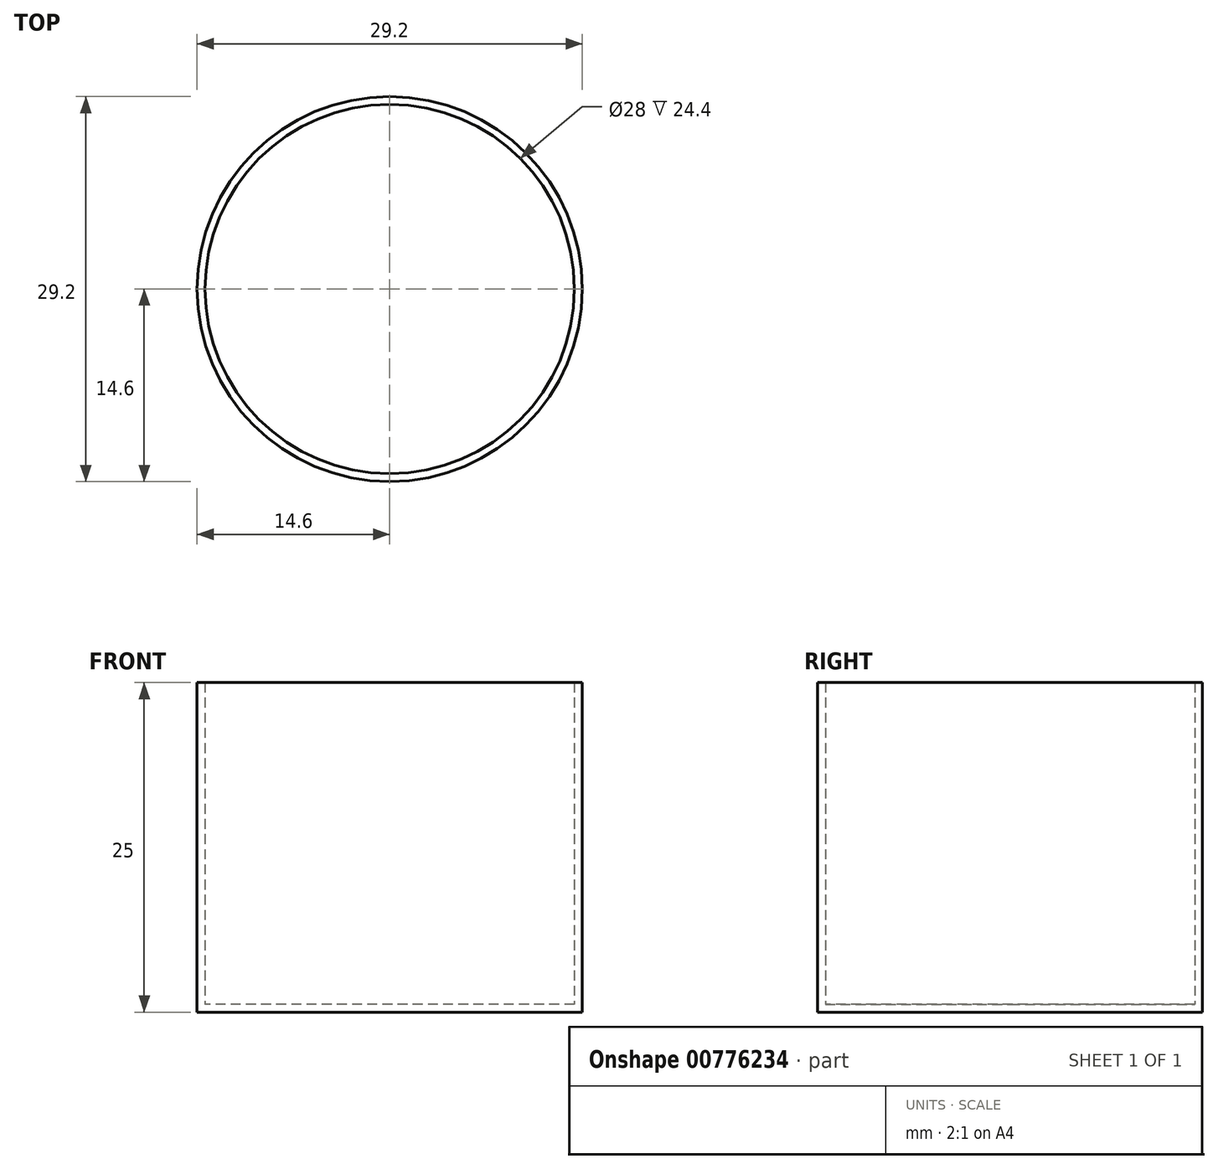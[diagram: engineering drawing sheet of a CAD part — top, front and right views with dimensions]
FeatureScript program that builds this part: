
annotation { "Feature Type Name" : "Feature", "Feature Type Description" : "" }
export const myFeature = defineFeature(function(context is Context, id is Id, definition is map)
    precondition{}
    {
        {
            var Q0;
            Q0=qCreatedBy(makeId("Top.planeOp"),FACE);
            var sketch = newSketch(context, id + "F0", { "sketchPlane" : qUnion([Q0])});
            skCircle(sketch, "E0", {"center": v(0, 0) * mm, "radius": 14.6 * mm});
            skCircle(sketch, "E1", {"center": v(0, 0) * mm, "radius": 14 * mm});
            skSolve(sketch);
        }
        {
            var Q0;
            Q0=makeQuery(id+"F0.imprint","IMPRINT",FACE,{"disambiguationData":[TD([[makeQuery(id+"F0.imprint","IMPRINT",EDGE,{"derivedFrom":sQuery(id+"F0.wireOp",EDGE,"E1")}),1.0]])]});
            var Q1;
            Q1=makeQuery(id+"F0.imprint","IMPRINT",FACE,{"disambiguationData":[TD([[makeQuery(id+"F0.imprint","IMPRINT",EDGE,{"derivedFrom":sQuery(id+"F0.wireOp",EDGE,"E0")}),1.0]])]});
            extrude(context, id + "F1", {"entities" : qUnion([Q0, Q1]), "depth" : .6 * mm, "offsetDistance" : 25 * mm});
        }
        {
            var Q0;
            Q0 = qSketchRegion(id + "F0", true);
            extrude(context, id + "F2", {"entities" : qUnion([Q0]), "operationType" : NewBodyOperationType.ADD, "depth" : 25 * mm, "offsetDistance" : 25 * mm});
        }
    });
